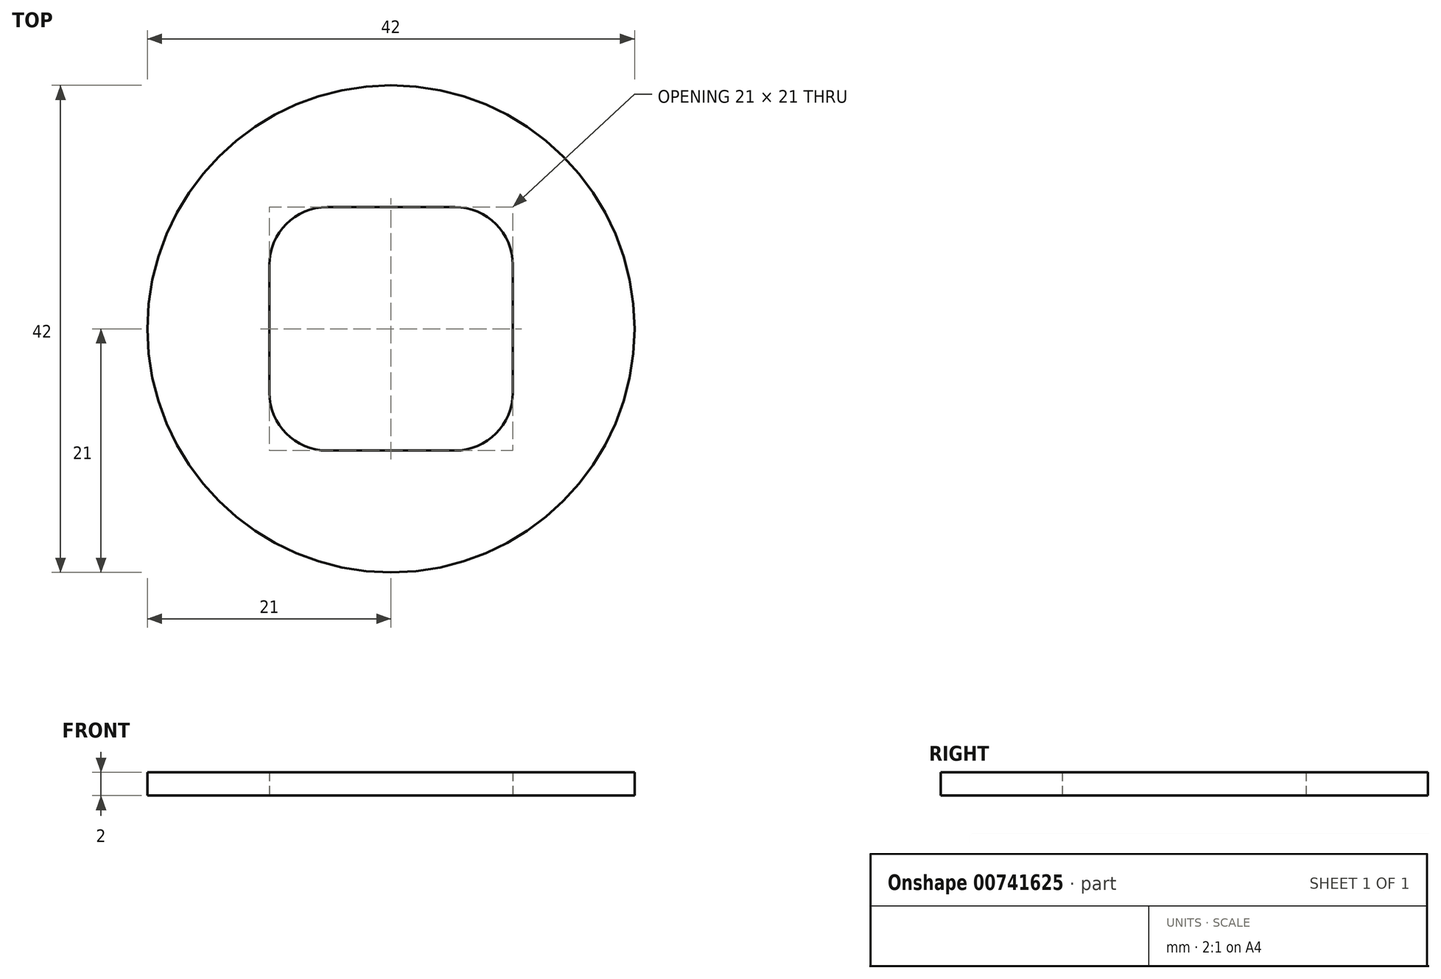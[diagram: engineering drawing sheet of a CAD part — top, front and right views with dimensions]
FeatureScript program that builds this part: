
annotation { "Feature Type Name" : "Feature", "Feature Type Description" : "" }
export const myFeature = defineFeature(function(context is Context, id is Id, definition is map)
    precondition{}
    {
        {
            var Q0;
            Q0=qCreatedBy(makeId("Top.planeOp"),FACE);
            var sketch = newSketch(context, id + "F0", { "sketchPlane" : qUnion([Q0])});
            skCircle(sketch, "E0", {"center": v(0, 0) * mm, "radius": 21 * mm});
            skLineSegment(sketch, "E1.bottom", {"start": v(-5.5, -10.5) * mm, "end": v(5.5, -10.5) * mm});
            skLineSegment(sketch, "E1.top", {"start": v(-5.5, 10.5) * mm, "end": v(5.5, 10.5) * mm});
            skLineSegment(sketch, "E1.left", {"start": v(-10.5, -5.5) * mm, "end": v(-10.5, 5.5) * mm});
            skLineSegment(sketch, "E1.right", {"start": v(10.5, -5.5) * mm, "end": v(10.5, 5.5) * mm});
            skPoint(sketch, "E2.visualSharp", {"position": v(-10.5, 10.5) * mm});
            skArc(sketch, "E2.filletArc", {"start": v(-5.5, 10.5) * mm, "mid": v(-9.04, 9.04) * mm, "end": v(-10.5, 5.5) * mm});
            skPoint(sketch, "E3.visualSharp", {"position": v(10.5, 10.5) * mm});
            skArc(sketch, "E3.filletArc", {"start": v(10.5, 5.5) * mm, "mid": v(9.04, 9.04) * mm, "end": v(5.5, 10.5) * mm});
            skPoint(sketch, "E4.visualSharp", {"position": v(10.5, -10.5) * mm});
            skArc(sketch, "E4.filletArc", {"start": v(5.5, -10.5) * mm, "mid": v(9.04, -9.04) * mm, "end": v(10.5, -5.5) * mm});
            skPoint(sketch, "E5.visualSharp", {"position": v(-10.5, -10.5) * mm});
            skArc(sketch, "E5.filletArc", {"start": v(-10.5, -5.5) * mm, "mid": v(-9.04, -9.04) * mm, "end": v(-5.5, -10.5) * mm});
            skSolve(sketch);
        }
        {
            var Q0;
            Q0=makeQuery(id+"F0.imprint","IMPRINT",FACE,{"disambiguationData":[TD([[makeQuery(id+"F0.imprint","IMPRINT",EDGE,{"derivedFrom":sQuery(id+"F0.wireOp",EDGE,"E0")}),1.0]])]});
            extrude(context, id + "F1", {"entities" : qUnion([Q0]), "depth" : 2 * mm, "offsetDistance" : 25 * mm});
        }
    });
